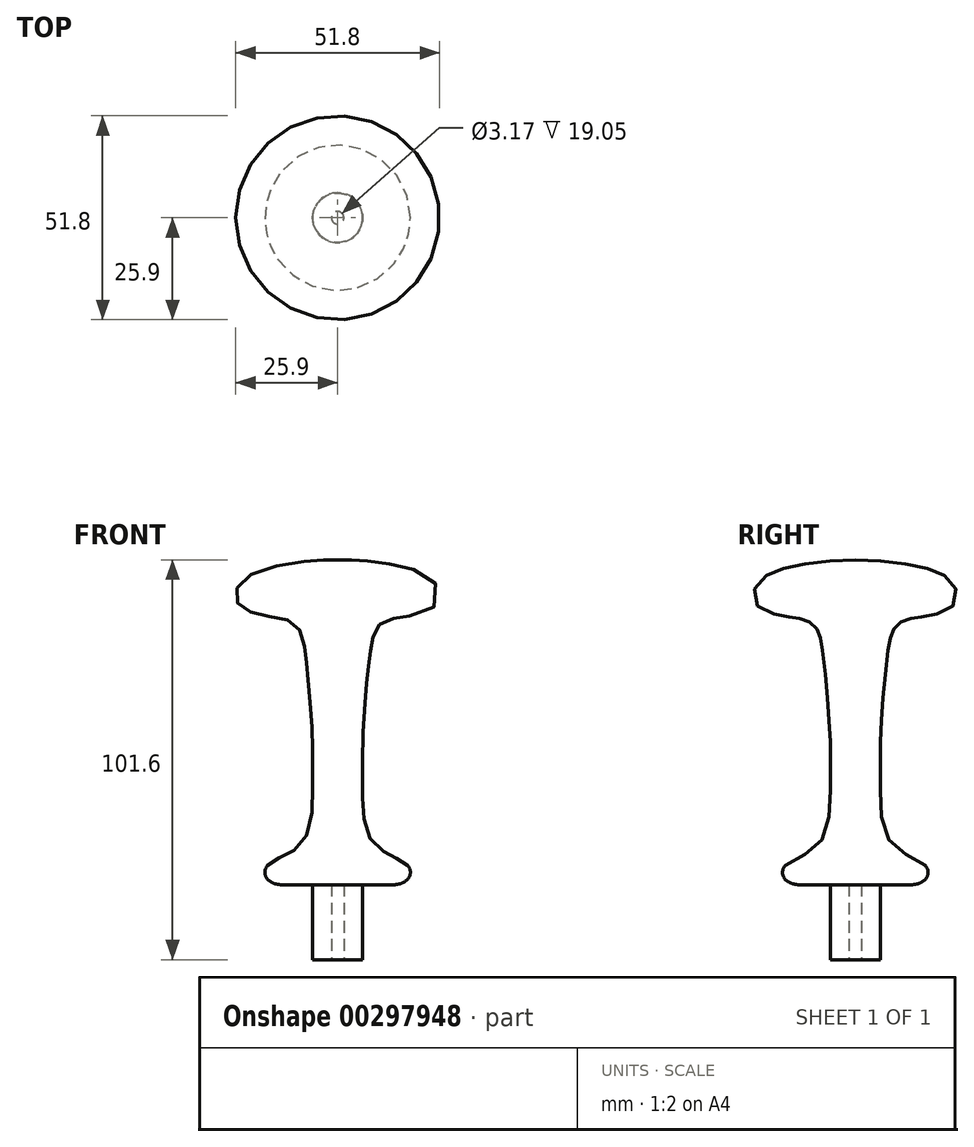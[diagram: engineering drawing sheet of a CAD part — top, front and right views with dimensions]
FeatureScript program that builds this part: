
annotation { "Feature Type Name" : "Feature", "Feature Type Description" : "" }
export const myFeature = defineFeature(function(context is Context, id is Id, definition is map)
    precondition{}
    {
        {
            var Q0;
            Q0=qCreatedBy(makeId("Front.planeOp"),FACE);
            var sketch = newSketch(context, id + "F0", { "sketchPlane" : qUnion([Q0])});
            skLineSegment(sketch, "E0", {"start": v(0, 0) * mm, "end": v(-6.35, 0) * mm});
            skLineSegment(sketch, "E1", {"start": v(-6.35, 0) * mm, "end": v(-6.35, 19.05) * mm});
            skLineSegment(sketch, "E2", {"start": v(-6.35, 19.05) * mm, "end": v(-19.05, 19.05) * mm});
            skLineSegment(sketch, "E3", {"start": v(-19.05, 19.05) * mm, "end": v(-19.05, 22.23) * mm});
            skLineSegment(sketch, "E4", {"start": v(0, 0) * mm, "end": v(0, 101.6) * mm, "construction": true});
            skLineSegment(sketch, "E5", {"start": v(7.26, 0) * mm, "end": v(7.26, 63.5) * mm, "construction": true});
            skLineSegment(sketch, "E6", {"start": v(1.87, 0) * mm, "end": v(3.87, 101.58) * mm, "construction": true});
            skLineSegment(sketch, "E7", {"start": v(-6.35, 19.05) * mm, "end": v(-6.35, 101.35) * mm, "construction": true});
            skPoint(sketch, "E8.2.internal.snap0", {"position": v(-12.7, 19.05) * mm});
            skFitSpline(sketch, "E9", {"points": [v(-19.05, 22.23) * mm, v(-14.91, 25.8) * mm, v(-8.24, 30.82) * mm, v(-6.35, 46.07) * mm, v(-6.35, 54.81) * mm, v(-7.39, 70.27) * mm, v(-8.23, 77.74) * mm, v(-10.51, 84.98) * mm, v(-18.66, 87.42) * mm, v(-25.4, 90.66) * mm, v(-23.7, 96.82) * mm, v(-6.35, 101.35) * mm, v(0, 101.6) * mm], "startDerivative": vector(58.39, 97.21) * mm, "endDerivative": vector(83.9, 0.38) * mm});
            skPoint(sketch, "E10", {"position": v(-6.35, 60.2) * mm});
            skLineSegment(sketch, "E11", {"start": v(0, 0) * mm, "end": v(0, 101.6) * mm});
            skLineSegment(sketch, "E12", {"start": v(-25.4, 90.66) * mm, "end": v(0, 90.16) * mm, "construction": true});
            skSolve(sketch);
        }
        {
            var Q0;
            Q0=makeQuery(id+"F0.imprint","IMPRINT",FACE,{"disambiguationData":[TD([[makeQuery(id+"F0.imprint","IMPRINT",EDGE,{"derivedFrom":sQuery(id+"F0.wireOp",EDGE,"E0")}),-1.0]])]});
            var Q1;
            Q1=sQuery(id+"F0.wireOp",EDGE,"E11");
            revolve(context, id + "F1", {"entities" : qUnion([Q0]), "axis" : qUnion([Q1]), "revolveType" : RevolveType.FULL});
        }
        {
            var Q0;
            Q0=makeQuery(id+"F1.opRevolve","SWEPT_EDGE",EDGE,{"disambiguationData":[OSD([sQuery(id+"F0.wireOp",EDGE,"E2"),sQuery(id+"F0.wireOp",EDGE,"E3")])]});
            fillet(context, id + "F2", {"entities" : qUnion([Q0]), "radius" : 5.08 * mm, "tangentPropagation" : true, "allowEdgeOverflow" : false});
        }
        {
            var Q0;
            Q0=makeQuery(id+"F2.opFillet","BLEND_EDGE",EDGE,{"blendedFrom":[makeQuery(id+"F1.opRevolve","SWEPT_EDGE",EDGE,{"disambiguationData":[OSD([sQuery(id+"F0.wireOp",EDGE,"E2"),sQuery(id+"F0.wireOp",EDGE,"E3")])]}),makeQuery(id+"F1.opRevolve","SWEPT_FACE",FACE,{"disambiguationData":[OSD([sQuery(id+"F0.wireOp",EDGE,"E9")])]})],"blendedInto":[makeQuery(id+"F1.opRevolve","SWEPT_FACE",FACE,{"disambiguationData":[OSD([sQuery(id+"F0.wireOp",EDGE,"E9")])]})]});
            fillet(context, id + "F3", {"entities" : qUnion([Q0]), "radius" : 2.54 * mm, "tangentPropagation" : true, "allowEdgeOverflow" : false});
        }
        {
            var Q0;
            Q0=makeQuery(id+"F1.opRevolve","SWEPT_FACE",FACE,{"disambiguationData":[OSD([sQuery(id+"F0.wireOp",EDGE,"E0")])]});
            var sketch = newSketch(context, id + "F4", { "sketchPlane" : qUnion([Q0])});
            skCircle(sketch, "E13", {"center": v(0, 0) * mm, "radius": 1.59 * mm});
            skSolve(sketch);
        }
        {
            var Q0;
            Q0 = qSketchRegion(id + "F4", true);
            extrude(context, id + "F5", {"entities" : qUnion([Q0]), "operationType" : NewBodyOperationType.REMOVE, "oppositeDirection" : true, "depth" : 19.05 * mm});
        }
    });
